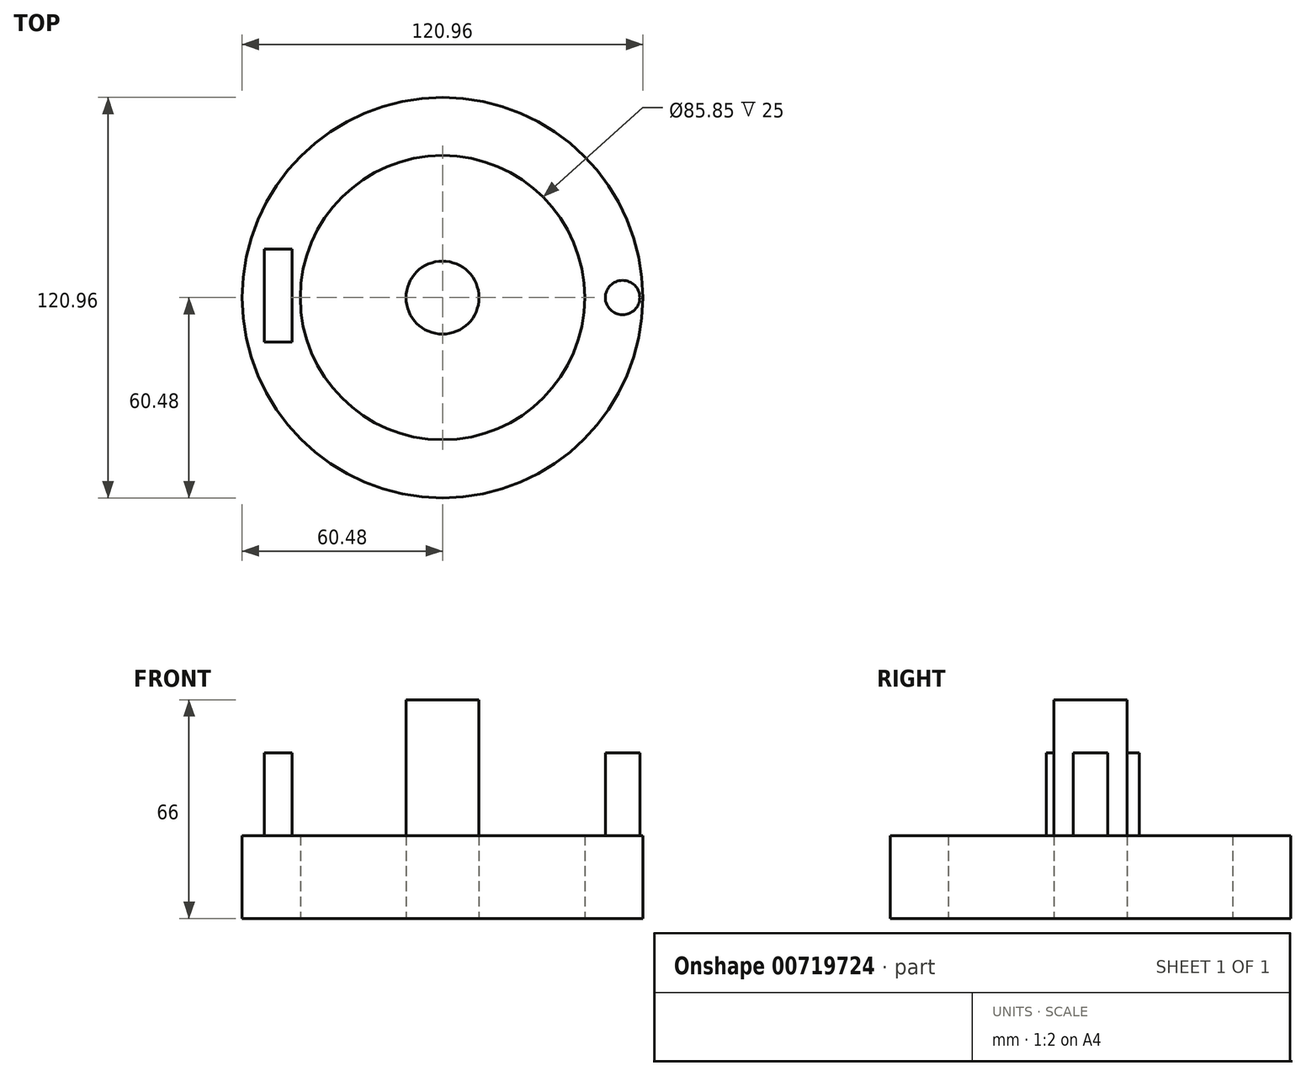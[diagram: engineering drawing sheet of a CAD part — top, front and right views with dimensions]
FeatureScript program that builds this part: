
annotation { "Feature Type Name" : "Feature", "Feature Type Description" : "" }
export const myFeature = defineFeature(function(context is Context, id is Id, definition is map)
    precondition{}
    {
        {
            var Q0;
            Q0=qCreatedBy(makeId("Top.planeOp"),FACE);
            var sketch = newSketch(context, id + "F0", { "sketchPlane" : qUnion([Q0])});
            skCircle(sketch, "E0", {"center": v(0, 0) * mm, "radius": 42.93 * mm});
            skCircle(sketch, "E1", {"center": v(0, 0) * mm, "radius": 11.02 * mm});
            skCircle(sketch, "E2", {"center": v(0, 0) * mm, "radius": 60.48 * mm});
            skSolve(sketch);
        }
        {
            var Q0;
            Q0=makeQuery(id+"F0.imprint","IMPRINT",FACE,{"disambiguationData":[TD([[makeQuery(id+"F0.imprint","IMPRINT",EDGE,{"derivedFrom":sQuery(id+"F0.wireOp",EDGE,"E1")}),1.0]])]});
            extrude(context, id + "F1", {"entities" : qUnion([Q0]), "depth" : 66 * mm, "offsetDistance" : 25 * mm});
        }
        {
            var Q0;
            Q0=qSketchRegion(id+"F0",true);
            extrude(context, id + "F2", {"entities" : qUnion([Q0]), "depth" : 25 * mm, "offsetDistance" : 25 * mm});
        }
        {
            var Q0;
            Q0=makeQuery(id+"F2.opExtrude","CAP_FACE",FACE,{"disambiguationData":[OSD([sQuery(id+"F0.wireOp",EDGE,"E0"),sQuery(id+"F0.wireOp",EDGE,"E2")])],"isStart":false});
            var sketch = newSketch(context, id + "F3", { "sketchPlane" : qUnion([Q0])});
            skLineSegment(sketch, "E3.bottom", {"start": v(-45.42, 14.7) * mm, "end": v(-53.75, 14.7) * mm});
            skLineSegment(sketch, "E3.top", {"start": v(-45.42, -13.38) * mm, "end": v(-53.75, -13.38) * mm});
            skLineSegment(sketch, "E3.left", {"start": v(-45.42, 14.7) * mm, "end": v(-45.42, -13.38) * mm});
            skLineSegment(sketch, "E3.right", {"start": v(-53.75, 14.7) * mm, "end": v(-53.75, -13.38) * mm});
            skSolve(sketch);
        }
        {
            var Q0;
            Q0=makeQuery(id+"F3.imprint","IMPRINT",FACE,{"disambiguationData":[TD([[makeQuery(id+"F3.imprint","IMPRINT",EDGE,{"derivedFrom":sQuery(id+"F3.wireOp",EDGE,"E3.bottom")}),1.0]])]});
            extrude(context, id + "F4", {"entities" : qUnion([Q0]), "operationType" : NewBodyOperationType.ADD, "depth" : 25 * mm, "offsetDistance" : 25 * mm});
        }
        {
            var Q0;
            Q0=makeQuery(id+"F2.opExtrude","CAP_FACE",FACE,{"disambiguationData":[OSD([sQuery(id+"F0.wireOp",EDGE,"E0"),sQuery(id+"F0.wireOp",EDGE,"E2")])],"isStart":false});
            var sketch = newSketch(context, id + "F5", { "sketchPlane" : qUnion([Q0])});
            skCircle(sketch, "E4", {"center": v(54.35, 0) * mm, "radius": 5.2 * mm});
            skSolve(sketch);
        }
        {
            var Q0;
            Q0=makeQuery(id+"F5.imprint","IMPRINT",FACE,{"disambiguationData":[TD([[makeQuery(id+"F5.imprint","IMPRINT",EDGE,{"derivedFrom":sQuery(id+"F5.wireOp",EDGE,"E4")}),1.0]])]});
            extrude(context, id + "F6", {"entities" : qUnion([Q0]), "operationType" : NewBodyOperationType.ADD, "depth" : 25 * mm, "offsetDistance" : 25 * mm});
        }
    });
